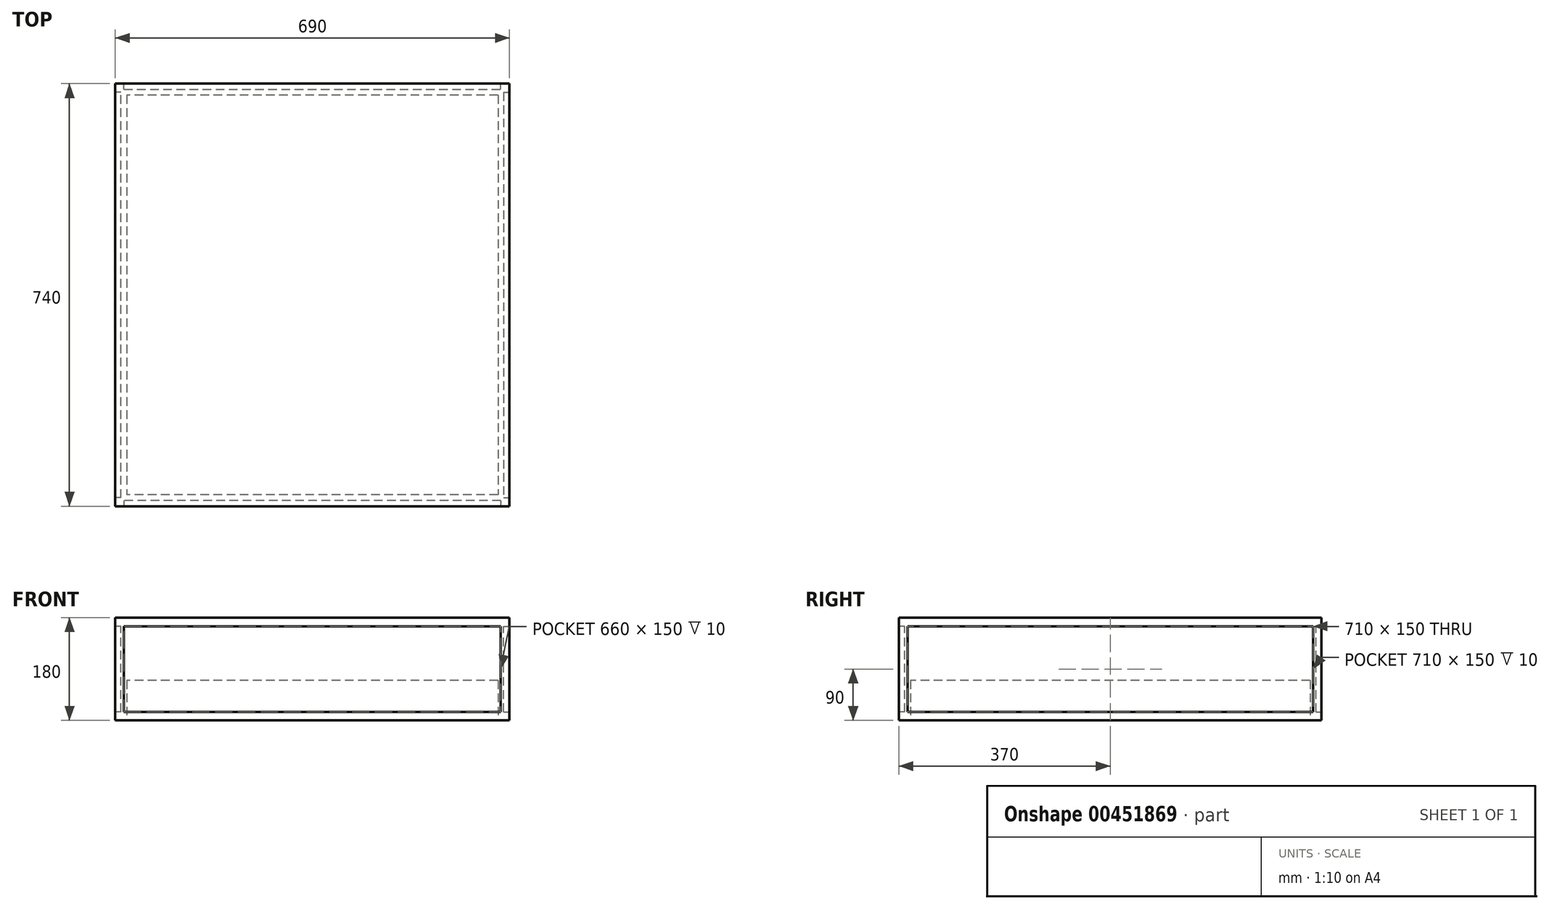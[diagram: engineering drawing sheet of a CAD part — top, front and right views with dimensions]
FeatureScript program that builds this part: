
annotation { "Feature Type Name" : "Feature", "Feature Type Description" : "" }
export const myFeature = defineFeature(function(context is Context, id is Id, definition is map)
    precondition{}
    {
        {
            var Q0;
            Q0=qCreatedBy(makeId("Top.planeOp"),FACE);
            var sketch = newSketch(context, id + "F0", { "sketchPlane" : qUnion([Q0])});
            skLineSegment(sketch, "E0.bottom", {"start": v(345, -370) * mm, "end": v(-345, -370) * mm});
            skLineSegment(sketch, "E0.top", {"start": v(345, 370) * mm, "end": v(-345, 370) * mm});
            skLineSegment(sketch, "E0.left", {"start": v(345, -370) * mm, "end": v(345, 370) * mm});
            skLineSegment(sketch, "E0.right", {"start": v(-345, -370) * mm, "end": v(-345, 370) * mm});
            skPoint(sketch, "E0.middle", {"position": v(0, 0) * mm});
            skSolve(sketch);
        }
        {
            var Q0;
            Q0 = qSketchRegion(id + "F0", true);
            var Q1;
            Q1=makeQuery(id+"F0.imprint","IMPRINT",FACE,{"disambiguationData":[TD([[makeQuery(id+"F0.imprint","IMPRINT",EDGE,{"derivedFrom":sQuery(id+"F0.wireOp",EDGE,"E0.bottom")}),-1.0]])]});
            extrude(context, id + "F1", {"entities" : qUnion([Q0, Q1]), "depth" : 180 * mm});
        }
        {
            var Q0;
            Q0=makeQuery(id+"F1.opExtrude","CAP_FACE",FACE,{"disambiguationData":[OSD([sQuery(id+"F0.wireOp",EDGE,"E0.bottom"),sQuery(id+"F0.wireOp",EDGE,"E0.top"),sQuery(id+"F0.wireOp",EDGE,"E0.left"),sQuery(id+"F0.wireOp",EDGE,"E0.right")])],"isStart":true});
            var sketch = newSketch(context, id + "F2", { "sketchPlane" : qUnion([Q0])});
            skLineSegment(sketch, "E1.bottom", {"start": v(325, -350) * mm, "end": v(-325, -350) * mm});
            skLineSegment(sketch, "E1.top", {"start": v(325, 350) * mm, "end": v(-325, 350) * mm});
            skLineSegment(sketch, "E1.left", {"start": v(325, -350) * mm, "end": v(325, 350) * mm});
            skLineSegment(sketch, "E1.right", {"start": v(-325, -350) * mm, "end": v(-325, 350) * mm});
            skPoint(sketch, "E1.middle", {"position": v(0, 0) * mm});
            skSolve(sketch);
        }
        {
            var Q0;
            Q0=makeQuery(id+"F2.imprint","IMPRINT",FACE,{"disambiguationData":[TD([[makeQuery(id+"F2.imprint","IMPRINT",EDGE,{"derivedFrom":sQuery(id+"F2.wireOp",EDGE,"E1.bottom")}),-1.0]])]});
            extrude(context, id + "F3", {"entities" : qUnion([Q0]), "operationType" : NewBodyOperationType.REMOVE, "oppositeDirection" : true, "depth" : 70 * mm});
        }
        {
            var Q0;
            Q0=makeQuery(id+"F1.opExtrude","SWEPT_FACE",FACE,{"disambiguationData":[OSD([sQuery(id+"F0.wireOp",EDGE,"E0.bottom")])]});
            var sketch = newSketch(context, id + "F4", { "sketchPlane" : qUnion([Q0])});
            skLineSegment(sketch, "E2.bottom", {"start": v(330, 15) * mm, "end": v(-330, 15) * mm});
            skLineSegment(sketch, "E2.top", {"start": v(330, 165) * mm, "end": v(-330, 165) * mm});
            skLineSegment(sketch, "E2.left", {"start": v(330, 15) * mm, "end": v(330, 165) * mm});
            skLineSegment(sketch, "E2.right", {"start": v(-330, 15) * mm, "end": v(-330, 165) * mm});
            skPoint(sketch, "E2.middle", {"position": v(0, 90) * mm});
            skPoint(sketch, "E2.middle.positionSnap0", {"position": v(-345, 90) * mm});
            skPoint(sketch, "E2.middle.positionSnap1", {"position": v(0, 180) * mm});
            skPoint(sketch, "E2.centerSnap0", {"position": v(-345, 90) * mm});
            skPoint(sketch, "E2.centerSnap1", {"position": v(0, 180) * mm});
            skSolve(sketch);
        }
        {
            var Q0;
            Q0=makeQuery(id+"F1.opExtrude","SWEPT_FACE",FACE,{"disambiguationData":[OSD([sQuery(id+"F0.wireOp",EDGE,"E0.right")])]});
            var sketch = newSketch(context, id + "F5", { "sketchPlane" : qUnion([Q0])});
            skLineSegment(sketch, "E3.bottom", {"start": v(355, 15) * mm, "end": v(-355, 15) * mm});
            skLineSegment(sketch, "E3.top", {"start": v(355, 165) * mm, "end": v(-355, 165) * mm});
            skLineSegment(sketch, "E3.left", {"start": v(355, 15) * mm, "end": v(355, 165) * mm});
            skLineSegment(sketch, "E3.right", {"start": v(-355, 15) * mm, "end": v(-355, 165) * mm});
            skPoint(sketch, "E3.middle", {"position": v(0, 90) * mm});
            skPoint(sketch, "E3.middle.positionSnap0", {"position": v(-370, 90) * mm});
            skPoint(sketch, "E3.middle.positionSnap1", {"position": v(0, 180) * mm});
            skPoint(sketch, "E3.centerSnap0", {"position": v(-370, 90) * mm});
            skPoint(sketch, "E3.centerSnap1", {"position": v(0, 180) * mm});
            skSolve(sketch);
        }
        {
            var Q0;
            Q0=makeQuery(id+"F1.opExtrude","SWEPT_FACE",FACE,{"disambiguationData":[OSD([sQuery(id+"F0.wireOp",EDGE,"E0.left")])]});
            var sketch = newSketch(context, id + "F6", { "sketchPlane" : qUnion([Q0])});
            skLineSegment(sketch, "E4.bottom", {"start": v(355, 15) * mm, "end": v(-355, 15) * mm});
            skLineSegment(sketch, "E4.top", {"start": v(355, 165) * mm, "end": v(-355, 165) * mm});
            skLineSegment(sketch, "E4.left", {"start": v(355, 15) * mm, "end": v(355, 165) * mm});
            skLineSegment(sketch, "E4.right", {"start": v(-355, 15) * mm, "end": v(-355, 165) * mm});
            skPoint(sketch, "E4.middle", {"position": v(0, 90) * mm});
            skPoint(sketch, "E4.middle.positionSnap0", {"position": v(-370, 90) * mm});
            skPoint(sketch, "E4.middle.positionSnap1", {"position": v(0, 180) * mm});
            skPoint(sketch, "E4.centerSnap0", {"position": v(-370, 90) * mm});
            skPoint(sketch, "E4.centerSnap1", {"position": v(0, 180) * mm});
            skSolve(sketch);
        }
        {
            var Q0;
            Q0=makeQuery(id+"F1.opExtrude","SWEPT_FACE",FACE,{"disambiguationData":[OSD([sQuery(id+"F0.wireOp",EDGE,"E0.top")])]});
            var sketch = newSketch(context, id + "F7", { "sketchPlane" : qUnion([Q0])});
            skLineSegment(sketch, "E5.bottom", {"start": v(330, 15) * mm, "end": v(-330, 15) * mm});
            skLineSegment(sketch, "E5.top", {"start": v(330, 165) * mm, "end": v(-330, 165) * mm});
            skLineSegment(sketch, "E5.left", {"start": v(330, 15) * mm, "end": v(330, 165) * mm});
            skLineSegment(sketch, "E5.right", {"start": v(-330, 15) * mm, "end": v(-330, 165) * mm});
            skPoint(sketch, "E5.middle", {"position": v(0, 90) * mm});
            skPoint(sketch, "E5.middle.positionSnap0", {"position": v(-345, 90) * mm});
            skPoint(sketch, "E5.middle.positionSnap1", {"position": v(0, 180) * mm});
            skPoint(sketch, "E5.centerSnap0", {"position": v(-345, 90) * mm});
            skPoint(sketch, "E5.centerSnap1", {"position": v(0, 180) * mm});
            skSolve(sketch);
        }
        {
            var Q0;
            Q0=makeQuery(id+"F5.imprint","IMPRINT",FACE,{"disambiguationData":[TD([[makeQuery(id+"F5.imprint","IMPRINT",EDGE,{"derivedFrom":sQuery(id+"F5.wireOp",EDGE,"E3.bottom")}),-1.0]])]});
            extrude(context, id + "F8", {"entities" : qUnion([Q0]), "operationType" : NewBodyOperationType.REMOVE, "oppositeDirection" : true, "depth" : 10 * mm});
        }
        {
            var Q0;
            Q0=makeQuery(id+"F7.imprint","IMPRINT",FACE,{"disambiguationData":[TD([[makeQuery(id+"F7.imprint","IMPRINT",EDGE,{"derivedFrom":sQuery(id+"F7.wireOp",EDGE,"E5.bottom")}),-1.0]])]});
            extrude(context, id + "F9", {"entities" : qUnion([Q0]), "operationType" : NewBodyOperationType.REMOVE, "oppositeDirection" : true, "depth" : 10 * mm});
        }
        {
            var Q0;
            Q0=makeQuery(id+"F6.imprint","IMPRINT",FACE,{"disambiguationData":[TD([[makeQuery(id+"F6.imprint","IMPRINT",EDGE,{"derivedFrom":sQuery(id+"F6.wireOp",EDGE,"E4.bottom")}),-1.0]])]});
            extrude(context, id + "F10", {"entities" : qUnion([Q0]), "operationType" : NewBodyOperationType.REMOVE, "oppositeDirection" : true, "depth" : 10 * mm});
        }
        {
            var Q0;
            Q0=makeQuery(id+"F4.imprint","IMPRINT",FACE,{"disambiguationData":[TD([[makeQuery(id+"F4.imprint","IMPRINT",EDGE,{"derivedFrom":sQuery(id+"F4.wireOp",EDGE,"E2.bottom")}),-1.0]])]});
            extrude(context, id + "F11", {"entities" : qUnion([Q0]), "operationType" : NewBodyOperationType.REMOVE, "oppositeDirection" : true, "depth" : 10 * mm});
        }
    });
